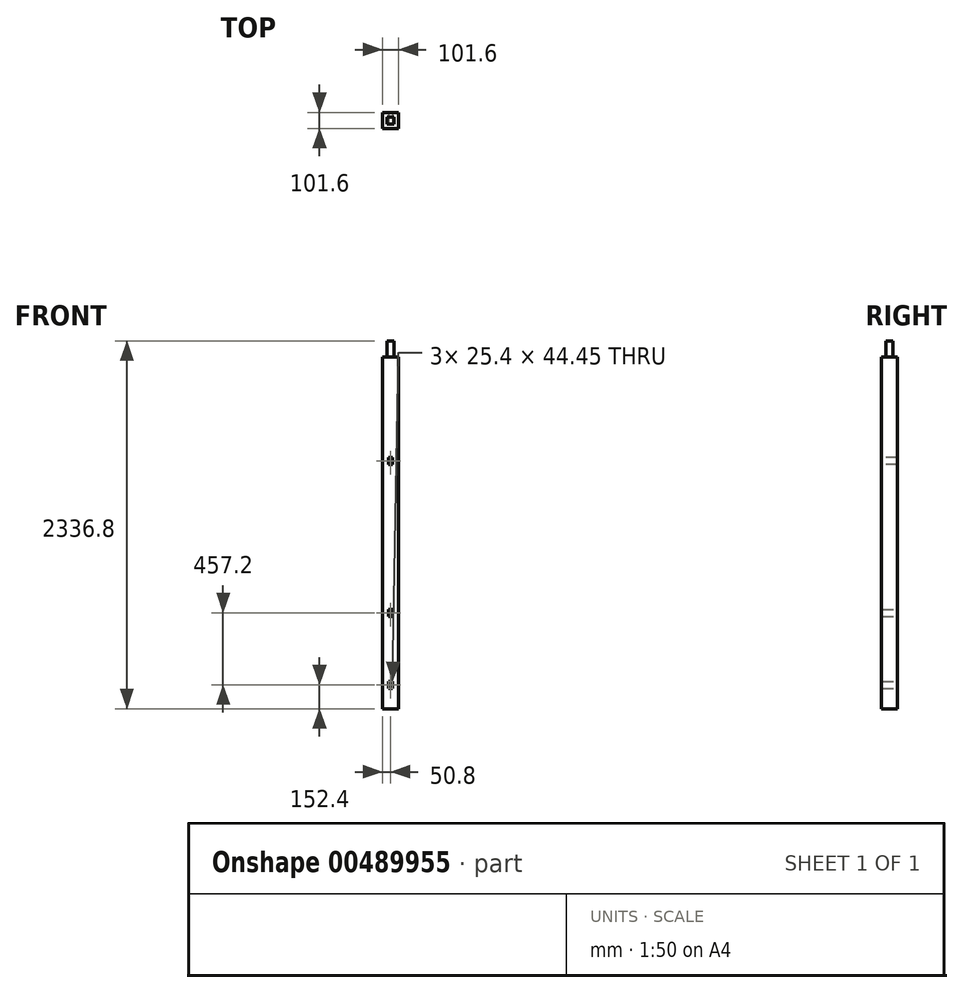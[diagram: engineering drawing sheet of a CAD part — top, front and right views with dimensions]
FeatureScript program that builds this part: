
annotation { "Feature Type Name" : "Feature", "Feature Type Description" : "" }
export const myFeature = defineFeature(function(context is Context, id is Id, definition is map)
    precondition{}
    {
        {
            var Q0;
            Q0=qCreatedBy(makeId("Top.planeOp"),FACE);
            var sketch = newSketch(context, id + "F0", { "sketchPlane" : qUnion([Q0])});
            skLineSegment(sketch, "E0.bottom", {"start": v(-50.8, 50.8) * mm, "end": v(50.8, 50.8) * mm});
            skLineSegment(sketch, "E0.top", {"start": v(-50.8, -50.8) * mm, "end": v(50.8, -50.8) * mm});
            skLineSegment(sketch, "E0.left", {"start": v(-50.8, 50.8) * mm, "end": v(-50.8, -50.8) * mm});
            skLineSegment(sketch, "E0.right", {"start": v(50.8, 50.8) * mm, "end": v(50.8, -50.8) * mm});
            skPoint(sketch, "E0.middle", {"position": v(0, 0) * mm});
            skSolve(sketch);
        }
        {
            var Q0;
            Q0 = qSketchRegion(id + "F0", true);
            extrude(context, id + "F1", {"entities" : qUnion([Q0]), "endBound" : BoundingType.SYMMETRIC, "depth" : 2336.8 * mm});
        }
        {
            var Q0;
            Q0=makeQuery(id+"F1.opExtrude","CAP_FACE",FACE,{"disambiguationData":[OSD([sQuery(id+"F0.wireOp",EDGE,"E0.bottom"),sQuery(id+"F0.wireOp",EDGE,"E0.top"),sQuery(id+"F0.wireOp",EDGE,"E0.left"),sQuery(id+"F0.wireOp",EDGE,"E0.right")])],"isStart":false});
            var sketch = newSketch(context, id + "F2", { "sketchPlane" : qUnion([Q0])});
            skLineSegment(sketch, "E1.bottom", {"start": v(-22.23, 22.23) * mm, "end": v(22.23, 22.23) * mm});
            skLineSegment(sketch, "E1.top", {"start": v(-22.23, -22.22) * mm, "end": v(22.23, -22.22) * mm});
            skLineSegment(sketch, "E1.left", {"start": v(-22.23, 22.23) * mm, "end": v(-22.23, -22.22) * mm});
            skLineSegment(sketch, "E1.right", {"start": v(22.23, 22.23) * mm, "end": v(22.22, -22.22) * mm});
            skPoint(sketch, "E1.middle", {"position": v(0, 0) * mm});
            skLineSegment(sketch, "E2.bottom", {"start": v(-50.8, 50.8) * mm, "end": v(50.8, 50.8) * mm});
            skLineSegment(sketch, "E2.top", {"start": v(-50.8, -50.8) * mm, "end": v(50.8, -50.8) * mm});
            skLineSegment(sketch, "E2.left", {"start": v(-50.8, 50.8) * mm, "end": v(-50.8, -50.8) * mm});
            skLineSegment(sketch, "E2.right", {"start": v(50.8, 50.8) * mm, "end": v(50.8, -50.8) * mm});
            skSolve(sketch);
        }
        {
            var Q0;
            Q0=makeQuery(id+"F2.imprint","IMPRINT",FACE,{"disambiguationData":[TD([[makeQuery(id+"F2.imprint","IMPRINT",EDGE,{"derivedFrom":sQuery(id+"F2.wireOp",EDGE,"E1.bottom")}),1.0]])]});
            extrude(context, id + "F3", {"entities" : qUnion([Q0]), "operationType" : NewBodyOperationType.REMOVE, "oppositeDirection" : true, "depth" : 101.6 * mm});
        }
        {
            var Q0;
            Q0=makeQuery(id+"F1.opExtrude","SWEPT_FACE",FACE,{"disambiguationData":[OSD([sQuery(id+"F0.wireOp",EDGE,"E0.top")])]});
            var sketch = newSketch(context, id + "F4", { "sketchPlane" : qUnion([Q0])});
            skLineSegment(sketch, "E3.bottom", {"start": v(-12.7, 384.18) * mm, "end": v(12.7, 384.18) * mm});
            skLineSegment(sketch, "E3.top", {"start": v(-12.7, 428.63) * mm, "end": v(12.7, 428.63) * mm});
            skLineSegment(sketch, "E3.left", {"start": v(-12.7, 384.18) * mm, "end": v(-12.7, 428.63) * mm});
            skLineSegment(sketch, "E3.right", {"start": v(12.7, 384.18) * mm, "end": v(12.7, 428.63) * mm});
            skPoint(sketch, "E3.middle", {"position": v(0, 406.4) * mm});
            skSolve(sketch);
        }
        {
            var Q0;
            Q0=makeQuery(id+"F4.imprint","IMPRINT",FACE,{"disambiguationData":[TD([[makeQuery(id+"F4.imprint","IMPRINT",EDGE,{"derivedFrom":sQuery(id+"F4.wireOp",EDGE,"E3.bottom")}),1.0]])]});
            extrude(context, id + "F5", {"entities" : qUnion([Q0]), "operationType" : NewBodyOperationType.REMOVE, "endBound" : BoundingType.THROUGH_ALL, "oppositeDirection" : true, "depth" : 25.4 * mm});
        }
        {
            var Q0;
            Q0=makeQuery(id+"F1.opExtrude","SWEPT_FACE",FACE,{"disambiguationData":[OSD([sQuery(id+"F0.wireOp",EDGE,"E0.bottom")])]});
            var sketch = newSketch(context, id + "F6", { "sketchPlane" : qUnion([Q0])});
            skLineSegment(sketch, "E4.bottom", {"start": v(-12.7, -581.02) * mm, "end": v(12.7, -581.02) * mm});
            skLineSegment(sketch, "E4.top", {"start": v(-12.7, -536.58) * mm, "end": v(12.7, -536.58) * mm});
            skLineSegment(sketch, "E4.left", {"start": v(-12.7, -581.02) * mm, "end": v(-12.7, -536.58) * mm});
            skLineSegment(sketch, "E4.right", {"start": v(12.7, -581.02) * mm, "end": v(12.7, -536.58) * mm});
            skPoint(sketch, "E4.middle", {"position": v(0, -558.8) * mm});
            skSolve(sketch);
        }
        {
            var Q0;
            Q0=makeQuery(id+"F6.imprint","IMPRINT",FACE,{"disambiguationData":[TD([[makeQuery(id+"F6.imprint","IMPRINT",EDGE,{"derivedFrom":sQuery(id+"F6.wireOp",EDGE,"E4.bottom")}),1.0]])]});
            extrude(context, id + "F7", {"entities" : qUnion([Q0]), "operationType" : NewBodyOperationType.REMOVE, "endBound" : BoundingType.THROUGH_ALL, "oppositeDirection" : true, "depth" : 25.4 * mm});
        }
        {
            var Q0;
            Q0=makeQuery(id+"F1.opExtrude","SWEPT_FACE",FACE,{"disambiguationData":[OSD([sQuery(id+"F0.wireOp",EDGE,"E0.bottom")])]});
            var sketch = newSketch(context, id + "F8", { "sketchPlane" : qUnion([Q0])});
            skLineSegment(sketch, "E5.bottom", {"start": v(-12.7, -993.77) * mm, "end": v(12.7, -993.77) * mm});
            skLineSegment(sketch, "E5.top", {"start": v(-12.7, -1038.22) * mm, "end": v(12.7, -1038.22) * mm});
            skLineSegment(sketch, "E5.left", {"start": v(-12.7, -993.77) * mm, "end": v(-12.7, -1038.22) * mm});
            skLineSegment(sketch, "E5.right", {"start": v(12.7, -993.77) * mm, "end": v(12.7, -1038.22) * mm});
            skPoint(sketch, "E5.middle", {"position": v(0, -1016) * mm});
            skSolve(sketch);
        }
        {
            var Q0;
            Q0=makeQuery(id+"F8.imprint","IMPRINT",FACE,{"disambiguationData":[TD([[makeQuery(id+"F8.imprint","IMPRINT",EDGE,{"derivedFrom":sQuery(id+"F8.wireOp",EDGE,"E5.bottom")}),-1.0]])]});
            extrude(context, id + "F9", {"entities" : qUnion([Q0]), "operationType" : NewBodyOperationType.REMOVE, "endBound" : BoundingType.THROUGH_ALL, "oppositeDirection" : true, "depth" : 25.4 * mm});
        }
    });
